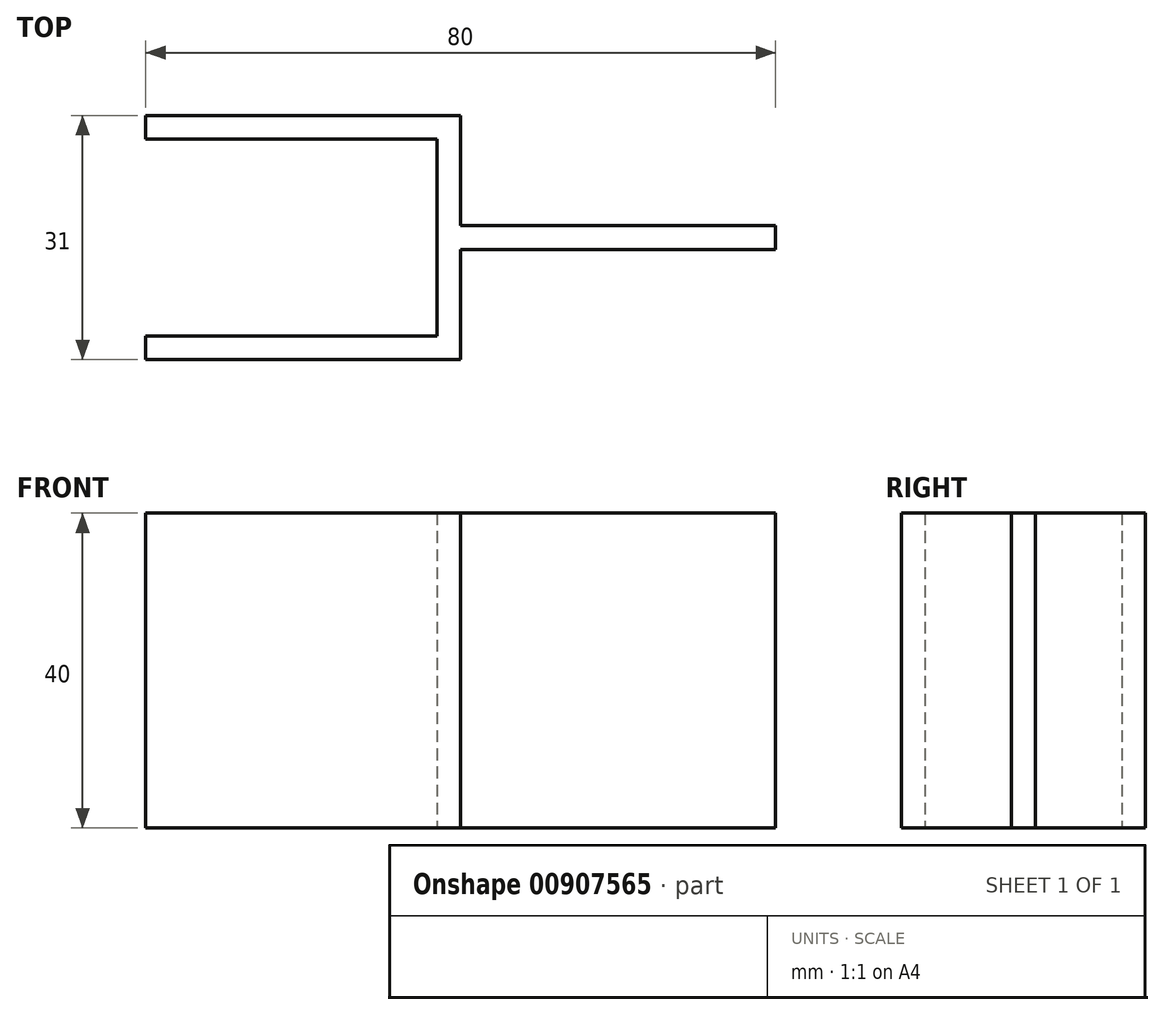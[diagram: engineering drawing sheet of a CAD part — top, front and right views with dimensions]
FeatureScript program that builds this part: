
annotation { "Feature Type Name" : "Feature", "Feature Type Description" : "" }
export const myFeature = defineFeature(function(context is Context, id is Id, definition is map)
    precondition{}
    {
        {
            var Q0;
            Q0=qCreatedBy(makeId("Top.planeOp"),FACE);
            var sketch = newSketch(context, id + "F0", { "sketchPlane" : qUnion([Q0])});
            skLineSegment(sketch, "E0", {"start": v(-27.9, 31) * mm, "end": v(12.1, 31) * mm});
            skLineSegment(sketch, "E1", {"start": v(12.1, 31) * mm, "end": v(12.1, 17) * mm});
            skLineSegment(sketch, "E2", {"start": v(12.1, 17) * mm, "end": v(52.1, 17) * mm});
            skLineSegment(sketch, "E3", {"start": v(52.1, 17) * mm, "end": v(52.1, 14) * mm});
            skLineSegment(sketch, "E4", {"start": v(52.1, 14) * mm, "end": v(12.1, 14) * mm});
            skLineSegment(sketch, "E5", {"start": v(12.1, 14) * mm, "end": v(12.1, 0) * mm});
            skLineSegment(sketch, "E6", {"start": v(12.1, 0) * mm, "end": v(-27.9, 0) * mm});
            skLineSegment(sketch, "E7", {"start": v(-27.9, 0) * mm, "end": v(-27.9, 3) * mm});
            skLineSegment(sketch, "E8", {"start": v(-27.9, 3) * mm, "end": v(9.1, 3) * mm});
            skLineSegment(sketch, "E9", {"start": v(9.1, 3) * mm, "end": v(9.1, 28) * mm});
            skLineSegment(sketch, "E10", {"start": v(9.1, 28) * mm, "end": v(-27.9, 28) * mm});
            skLineSegment(sketch, "E11", {"start": v(-27.9, 28) * mm, "end": v(-27.9, 31) * mm});
            skSolve(sketch);
        }
        {
            var Q0;
            Q0=qSketchRegion(id+"F0",true);
            extrude(context, id + "F1", {"entities" : qUnion([Q0]), "depth" : 40 * mm, "offsetDistance" : 25 * mm});
        }
    });
